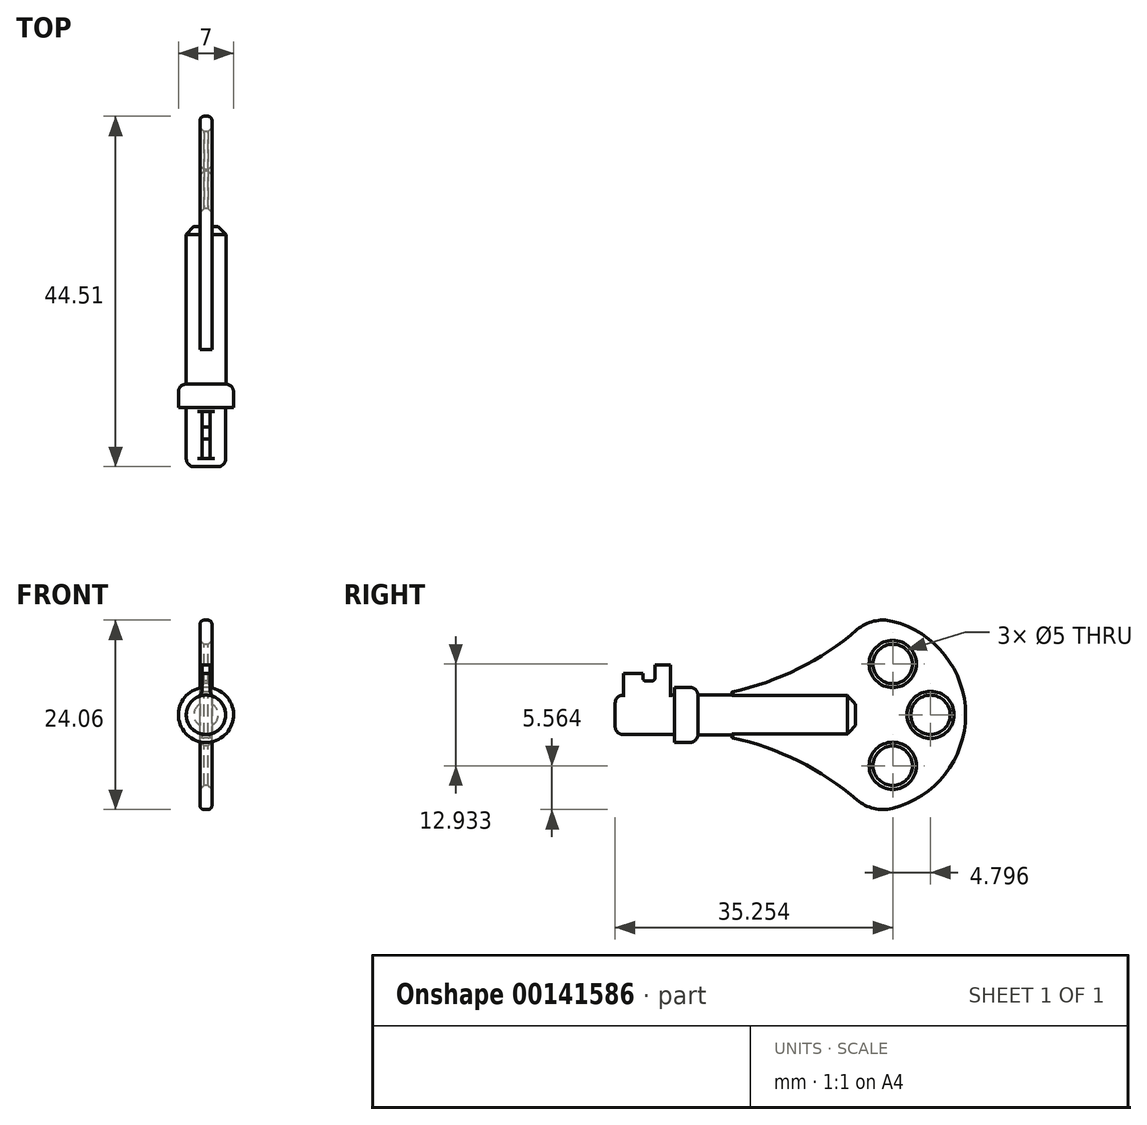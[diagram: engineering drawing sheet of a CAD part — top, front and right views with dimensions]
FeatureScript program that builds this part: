
annotation { "Feature Type Name" : "Feature", "Feature Type Description" : "" }
export const myFeature = defineFeature(function(context is Context, id is Id, definition is map)
    precondition{}
    {
        {
            var Q0;
            Q0=qCreatedBy(makeId("Front.planeOp"),FACE);
            var sketch = newSketch(context, id + "F0", { "sketchPlane" : qUnion([Q0])});
            skCircle(sketch, "E0", {"center": v(0, 0) * mm, "radius": 2.5 * mm});
            skSolve(sketch);
        }
        {
            var Q0;
            Q0=qSketchRegion(id+"F0",true);
            extrude(context, id + "F1", {"entities" : qUnion([Q0]), "depth" : 7.5 * mm});
        }
        {
            var Q0;
            Q0=makeQuery(id+"F1.opExtrude","CAP_EDGE",EDGE,{"disambiguationData":[OSD([sQuery(id+"F0.wireOp",EDGE,"E0")])],"isStart":false});
            fillet(context, id + "F2", {"entities" : qUnion([Q0]), "radius" : 1 * mm, "tangentPropagation" : true, "allowEdgeOverflow" : false});
        }
        {
            var Q0;
            Q0=qCreatedBy(makeId("Right.planeOp"),FACE);
            var sketch = newSketch(context, id + "F3", { "sketchPlane" : qUnion([Q0])});
            skLineSegment(sketch, "E1", {"start": v(-6.47, 2.29) * mm, "end": v(-6.47, 5.29) * mm});
            skLineSegment(sketch, "E2", {"start": v(-6.47, 5.29) * mm, "end": v(-3.97, 5.29) * mm});
            skLineSegment(sketch, "E3", {"start": v(-3.97, 5.29) * mm, "end": v(-3.97, 4.32) * mm});
            skLineSegment(sketch, "E4", {"start": v(-3.97, 4.32) * mm, "end": v(-2.47, 4.32) * mm});
            skLineSegment(sketch, "E5", {"start": v(-2.47, 4.32) * mm, "end": v(-2.47, 6.32) * mm});
            skLineSegment(sketch, "E6", {"start": v(-2.47, 6.32) * mm, "end": v(-0.47, 6.32) * mm});
            skLineSegment(sketch, "E7", {"start": v(-0.47, 6.32) * mm, "end": v(-0.47, 2.28) * mm});
            skLineSegment(sketch, "E8", {"start": v(-0.47, 2.28) * mm, "end": v(-6.47, 2.29) * mm});
            skLineSegment(sketch, "E9", {"start": v(0, 2.49) * mm, "end": v(-9, 2.5) * mm, "construction": true});
            skLineSegment(sketch, "E10", {"start": v(-6.47, 3.32) * mm, "end": v(-0.47, 3.32) * mm, "construction": true});
            skSolve(sketch);
        }
        {
            var Q0;
            Q0=qSketchRegion(id+"F3",true);
            extrude(context, id + "F4", {"entities" : qUnion([Q0]), "operationType" : NewBodyOperationType.ADD, "depth" : 1 * mm, "symmetric" : true});
        }
        {
            var Q0;
            Q0=makeQuery(id+"F4.opExtrude","SWEPT_EDGE",EDGE,{"disambiguationData":[OSD([sQuery(id+"F3.wireOp",EDGE,"E4"),sQuery(id+"F3.wireOp",EDGE,"E5")])]});
            var Q1;
            Q1=makeQuery(id+"F4.opExtrude","SWEPT_EDGE",EDGE,{"disambiguationData":[OSD([sQuery(id+"F3.wireOp",EDGE,"E3"),sQuery(id+"F3.wireOp",EDGE,"E4")])]});
            fillet(context, id + "F5", {"entities" : qUnion([Q0, Q1]), "radius" : .3 * mm, "tangentPropagation" : true, "allowEdgeOverflow" : false});
        }
        {
            var Q0;
            Q0=makeQuery(id+"F1.opExtrude","CAP_FACE",FACE,{"disambiguationData":[OSD([sQuery(id+"F0.wireOp",EDGE,"E0")])],"isStart":true});
            var sketch = newSketch(context, id + "F6", { "sketchPlane" : qUnion([Q0])});
            skCircle(sketch, "E11", {"center": v(0, 0) * mm, "radius": 3.5 * mm});
            skSolve(sketch);
        }
        {
            var Q0;
            Q0=qSketchRegion(id+"F6",true);
            extrude(context, id + "F7", {"entities" : qUnion([Q0]), "operationType" : NewBodyOperationType.ADD, "depth" : 3 * mm});
        }
        {
            var Q0;
            Q0=makeQuery(id+"F7.opExtrude","CAP_EDGE",EDGE,{"disambiguationData":[OSD([sQuery(id+"F6.wireOp",EDGE,"E11")])],"isStart":false});
            fillet(context, id + "F8", {"entities" : qUnion([Q0]), "radius" : 1 * mm, "tangentPropagation" : true, "allowEdgeOverflow" : false});
        }
        {
            var Q0;
            Q0=makeQuery(id+"F7.opExtrude","CAP_FACE",FACE,{"disambiguationData":[OSD([sQuery(id+"F6.wireOp",EDGE,"E11")])],"isStart":false});
            var sketch = newSketch(context, id + "F9", { "sketchPlane" : qUnion([Q0])});
            skCircle(sketch, "E12", {"center": v(0, 0) * mm, "radius": 2.55 * mm});
            skSolve(sketch);
        }
        {
            var Q0;
            Q0=qSketchRegion(id+"F9",true);
            extrude(context, id + "F10", {"entities" : qUnion([Q0]), "operationType" : NewBodyOperationType.ADD, "depth" : 20 * mm});
        }
        {
            var Q0;
            Q0=qCreatedBy(makeId("Right.planeOp"),FACE);
            var sketch = newSketch(context, id + "F11", { "sketchPlane" : qUnion([Q0])});
            skLineSegment(sketch, "E13", {"start": v(7.35, 0) * mm, "end": v(7.35, 2.92) * mm});
            skArc(sketch, "E14", {"start": v(7.35, 2.92) * mm, "mid": v(16.73, 6.35) * mm, "end": v(24.8, 12.24) * mm});
            skArc(sketch, "E15", {"start": v(37, 0) * mm, "mid": v(33.43, 8.64) * mm, "end": v(24.8, 12.24) * mm});
            skArc(sketch, "E16", {"start": v(35.05, 0) * mm, "mid": v(32.55, 2.5) * mm, "end": v(30.05, 0) * mm});
            skLineSegment(sketch, "E17.MirrorCS", {"start": v(29, 0) * mm, "end": v(29, 0) * mm});
            skCircle(sketch, "E18.MirrorC", {"center": v(27.75, 6.47) * mm, "radius": 2.5 * mm});
            skArc(sketch, "E19.MirrorCS", {"start": v(37, 0) * mm, "mid": v(33.43, -8.64) * mm, "end": v(24.8, -12.24) * mm});
            skArc(sketch, "E20.MirrorCS", {"start": v(7.35, -2.92) * mm, "mid": v(16.73, -6.35) * mm, "end": v(24.8, -12.24) * mm});
            skLineSegment(sketch, "E21.MirrorCS", {"start": v(7.35, 0) * mm, "end": v(7.35, -2.92) * mm});
            skCircle(sketch, "E22.MirrorC", {"center": v(27.75, -6.47) * mm, "radius": 2.5 * mm});
            skArc(sketch, "E23.MirrorCS", {"start": v(35.05, 0) * mm, "mid": v(32.55, -2.5) * mm, "end": v(30.05, 0) * mm});
            skSolve(sketch);
        }
        {
            var Q0;
            Q0=makeQuery(id+"F11.imprint","IMPRINT",FACE,{"disambiguationData":[TD([[makeQuery(id+"F11.imprint","IMPRINT",EDGE,{"derivedFrom":sQuery(id+"F11.wireOp",EDGE,"e2de7071-8971-4a5e-abbe-7816cc336ebe.trimOffspring")}),1.0]])]});
            var Q1;
            Q1=makeQuery(id+"F11.imprint","IMPRINT",FACE,{"disambiguationData":[TD([[makeQuery(id+"F11.imprint","IMPRINT",EDGE,{"derivedFrom":sQuery(id+"F11.wireOp",EDGE,"E13")}),-1.0]])]});
            extrude(context, id + "F12", {"entities" : qUnion([Q0, Q1]), "operationType" : NewBodyOperationType.ADD, "depth" : 1.5 * mm, "symmetric" : true});
        }
        {
            var Q0;
            Q0=makeQuery(id+"F12.opExtrude","SWEPT_EDGE",EDGE,{"disambiguationData":[OSD([sQuery(id+"F11.wireOp",EDGE,"E14"),sQuery(id+"F11.wireOp",EDGE,"E15")])]});
            var Q1;
            Q1=makeQuery(id+"F12.opExtrude","SWEPT_EDGE",EDGE,{"disambiguationData":[OSD([sQuery(id+"F11.wireOp",EDGE,"E19.MirrorCS"),sQuery(id+"F11.wireOp",EDGE,"E20.MirrorCS")])]});
            fillet(context, id + "F13", {"entities" : qUnion([Q0, Q1]), "radius" : 5 * mm, "tangentPropagation" : true, "allowEdgeOverflow" : false});
        }
        {
            var Q0;
            Q0=makeQuery(id+"F12.opExtrude","CAP_EDGE",EDGE,{"disambiguationData":[OSD([sQuery(id+"F11.wireOp",EDGE,"E15"),sQuery(id+"F11.wireOp",EDGE,"E19.MirrorCS")])],"isStart":false});
            var Q1;
            {var subQ0=sQuery(id+"F11.wireOp",EDGE,"E20.MirrorCS");var subQ1=sQuery(id+"F11.wireOp",EDGE,"E19.MirrorCS");Q1=makeQuery(id+"F13.opFillet","BLEND_EDGE",EDGE,{"blendedFrom":[makeQuery(id+"F12.opExtrude","SWEPT_EDGE",EDGE,{"disambiguationData":[OSD([subQ1,subQ0])]}),makeQuery(id+"F12.opExtrude","CAP_FACE",FACE,{"disambiguationData":[OSD([sQuery(id+"F11.wireOp",EDGE,"E13"),sQuery(id+"F11.wireOp",EDGE,"E14"),sQuery(id+"F11.wireOp",EDGE,"E15"),sQuery(id+"F11.wireOp",EDGE,"E16"),sQuery(id+"F11.wireOp",EDGE,"E18.MirrorC"),subQ1,subQ0,sQuery(id+"F11.wireOp",EDGE,"E21.MirrorCS"),sQuery(id+"F11.wireOp",EDGE,"E22.MirrorC"),sQuery(id+"F11.wireOp",EDGE,"E23.MirrorCS")])],"isStart":false})],"blendedInto":[makeQuery(id+"F12.opExtrude","CAP_FACE",FACE,{"disambiguationData":[OSD([sQuery(id+"F11.wireOp",EDGE,"E13"),sQuery(id+"F11.wireOp",EDGE,"E14"),sQuery(id+"F11.wireOp",EDGE,"E15"),sQuery(id+"F11.wireOp",EDGE,"E16"),sQuery(id+"F11.wireOp",EDGE,"E18.MirrorC"),subQ1,subQ0,sQuery(id+"F11.wireOp",EDGE,"E21.MirrorCS"),sQuery(id+"F11.wireOp",EDGE,"E22.MirrorC"),sQuery(id+"F11.wireOp",EDGE,"E23.MirrorCS")])],"isStart":false})]});}
            var Q2;
            Q2=makeQuery(id+"F12.opExtrude","CAP_EDGE",EDGE,{"disambiguationData":[OSD([sQuery(id+"F11.wireOp",EDGE,"E20.MirrorCS")])],"isStart":false});
            var Q3;
            Q3=makeQuery(id+"F12.opExtrude","CAP_EDGE",EDGE,{"disambiguationData":[OSD([sQuery(id+"F11.wireOp",EDGE,"E14")])],"isStart":true});
            var Q4;
            Q4=makeQuery(id+"F12.opExtrude","CAP_EDGE",EDGE,{"disambiguationData":[OSD([sQuery(id+"F11.wireOp",EDGE,"E20.MirrorCS")])],"isStart":true});
            var Q5;
            Q5=makeQuery(id+"F12.opExtrude","CAP_EDGE",EDGE,{"disambiguationData":[OSD([sQuery(id+"F11.wireOp",EDGE,"E15"),sQuery(id+"F11.wireOp",EDGE,"E19.MirrorCS")])],"isStart":true});
            fillet(context, id + "F14", {"entities" : qUnion([Q0, Q1, Q2, Q3, Q4, Q5]), "radius" : .5 * mm, "tangentPropagation" : true, "allowEdgeOverflow" : false});
        }
        {
            var Q0;
            Q0=makeQuery(id+"F12.opExtrude","CAP_EDGE",EDGE,{"disambiguationData":[OSD([sQuery(id+"F11.wireOp",EDGE,"E16"),sQuery(id+"F11.wireOp",EDGE,"E23.MirrorCS")])],"isStart":false});
            var Q1;
            Q1=makeQuery(id+"F12.opExtrude","CAP_EDGE",EDGE,{"disambiguationData":[OSD([sQuery(id+"F11.wireOp",EDGE,"E22.MirrorC")])],"isStart":false});
            var Q2;
            Q2=makeQuery(id+"F12.opExtrude","CAP_EDGE",EDGE,{"disambiguationData":[OSD([sQuery(id+"F11.wireOp",EDGE,"E18.MirrorC")])],"isStart":true});
            var Q3;
            Q3=makeQuery(id+"F12.opExtrude","CAP_EDGE",EDGE,{"disambiguationData":[OSD([sQuery(id+"F11.wireOp",EDGE,"E18.MirrorC")])],"isStart":false});
            var Q4;
            Q4=makeQuery(id+"F12.opExtrude","CAP_EDGE",EDGE,{"disambiguationData":[OSD([sQuery(id+"F11.wireOp",EDGE,"E16"),sQuery(id+"F11.wireOp",EDGE,"E23.MirrorCS")])],"isStart":true});
            var Q5;
            Q5=makeQuery(id+"F12.opExtrude","CAP_EDGE",EDGE,{"disambiguationData":[OSD([sQuery(id+"F11.wireOp",EDGE,"E22.MirrorC")])],"isStart":true});
            chamfer(context, id + "F15", {"entities" : qUnion([Q0, Q1, Q2, Q3, Q4, Q5]), "width" : .5 * mm, "tangentPropagation" : true});
        }
        {
            var Q0;
            {var subQ0=sQuery(id+"F9.wireOp",EDGE,"E12");Q0=makeQuery(id+"F12.boolean.opBoolean","SPLIT",EDGE,{"disambiguationData":[TD([makeQuery(id+"F12.opExtrude","CAP_FACE",FACE,{"disambiguationData":[OSD([sQuery(id+"F11.wireOp",EDGE,"E13"),sQuery(id+"F11.wireOp",EDGE,"E14"),sQuery(id+"F11.wireOp",EDGE,"E15"),sQuery(id+"F11.wireOp",EDGE,"E16"),sQuery(id+"F11.wireOp",EDGE,"E18.MirrorC"),sQuery(id+"F11.wireOp",EDGE,"E19.MirrorCS"),sQuery(id+"F11.wireOp",EDGE,"E20.MirrorCS"),sQuery(id+"F11.wireOp",EDGE,"E21.MirrorCS"),sQuery(id+"F11.wireOp",EDGE,"E22.MirrorC"),sQuery(id+"F11.wireOp",EDGE,"E23.MirrorCS")])],"isStart":false})])],"derivedFrom":makeQuery(id+"F10.opExtrude","CAP_EDGE",EDGE,{"disambiguationData":[OSD([subQ0])],"isStart":false})});}
            var Q1;
            {var subQ0=sQuery(id+"F9.wireOp",EDGE,"E12");Q1=makeQuery(id+"F12.boolean.opBoolean","SPLIT",EDGE,{"disambiguationData":[TD([makeQuery(id+"F12.opExtrude","CAP_FACE",FACE,{"disambiguationData":[OSD([sQuery(id+"F11.wireOp",EDGE,"E13"),sQuery(id+"F11.wireOp",EDGE,"E14"),sQuery(id+"F11.wireOp",EDGE,"E15"),sQuery(id+"F11.wireOp",EDGE,"E16"),sQuery(id+"F11.wireOp",EDGE,"E18.MirrorC"),sQuery(id+"F11.wireOp",EDGE,"E19.MirrorCS"),sQuery(id+"F11.wireOp",EDGE,"E20.MirrorCS"),sQuery(id+"F11.wireOp",EDGE,"E21.MirrorCS"),sQuery(id+"F11.wireOp",EDGE,"E22.MirrorC"),sQuery(id+"F11.wireOp",EDGE,"E23.MirrorCS")])],"isStart":true})])],"derivedFrom":makeQuery(id+"F10.opExtrude","CAP_EDGE",EDGE,{"disambiguationData":[OSD([subQ0])],"isStart":false})});}
            chamfer(context, id + "F16", {"entities" : qUnion([Q0, Q1]), "width" : 1 * mm, "tangentPropagation" : true});
        }
        {
            var Q0;
            Q0=makeQuery(id+"F4.boolean.opBoolean","INTERSECT",EDGE,{"derivedFrom":[makeQuery(id+"F1.opExtrude","SWEPT_FACE",FACE,{"disambiguationData":[OSD([sQuery(id+"F0.wireOp",EDGE,"E0")])]}),makeQuery(id+"F4.opExtrude","CAP_FACE",FACE,{"disambiguationData":[OSD([sQuery(id+"F3.wireOp",EDGE,"E1"),sQuery(id+"F3.wireOp",EDGE,"E2"),sQuery(id+"F3.wireOp",EDGE,"E3"),sQuery(id+"F3.wireOp",EDGE,"E4"),sQuery(id+"F3.wireOp",EDGE,"E5"),sQuery(id+"F3.wireOp",EDGE,"E6"),sQuery(id+"F3.wireOp",EDGE,"E7"),sQuery(id+"F3.wireOp",EDGE,"E8")])],"isStart":true})]});
            var Q1;
            Q1=makeQuery(id+"F4.boolean.opBoolean","INTERSECT",EDGE,{"derivedFrom":[makeQuery(id+"F1.opExtrude","SWEPT_FACE",FACE,{"disambiguationData":[OSD([sQuery(id+"F0.wireOp",EDGE,"E0")])]}),makeQuery(id+"F4.opExtrude","CAP_FACE",FACE,{"disambiguationData":[OSD([sQuery(id+"F3.wireOp",EDGE,"E1"),sQuery(id+"F3.wireOp",EDGE,"E2"),sQuery(id+"F3.wireOp",EDGE,"E3"),sQuery(id+"F3.wireOp",EDGE,"E4"),sQuery(id+"F3.wireOp",EDGE,"E5"),sQuery(id+"F3.wireOp",EDGE,"E6"),sQuery(id+"F3.wireOp",EDGE,"E7"),sQuery(id+"F3.wireOp",EDGE,"E8")])],"isStart":false})]});
            fillet(context, id + "F17", {"entities" : qUnion([Q0, Q1]), "radius" : 1 * mm, "tangentPropagation" : true, "allowEdgeOverflow" : false});
        }
    });
